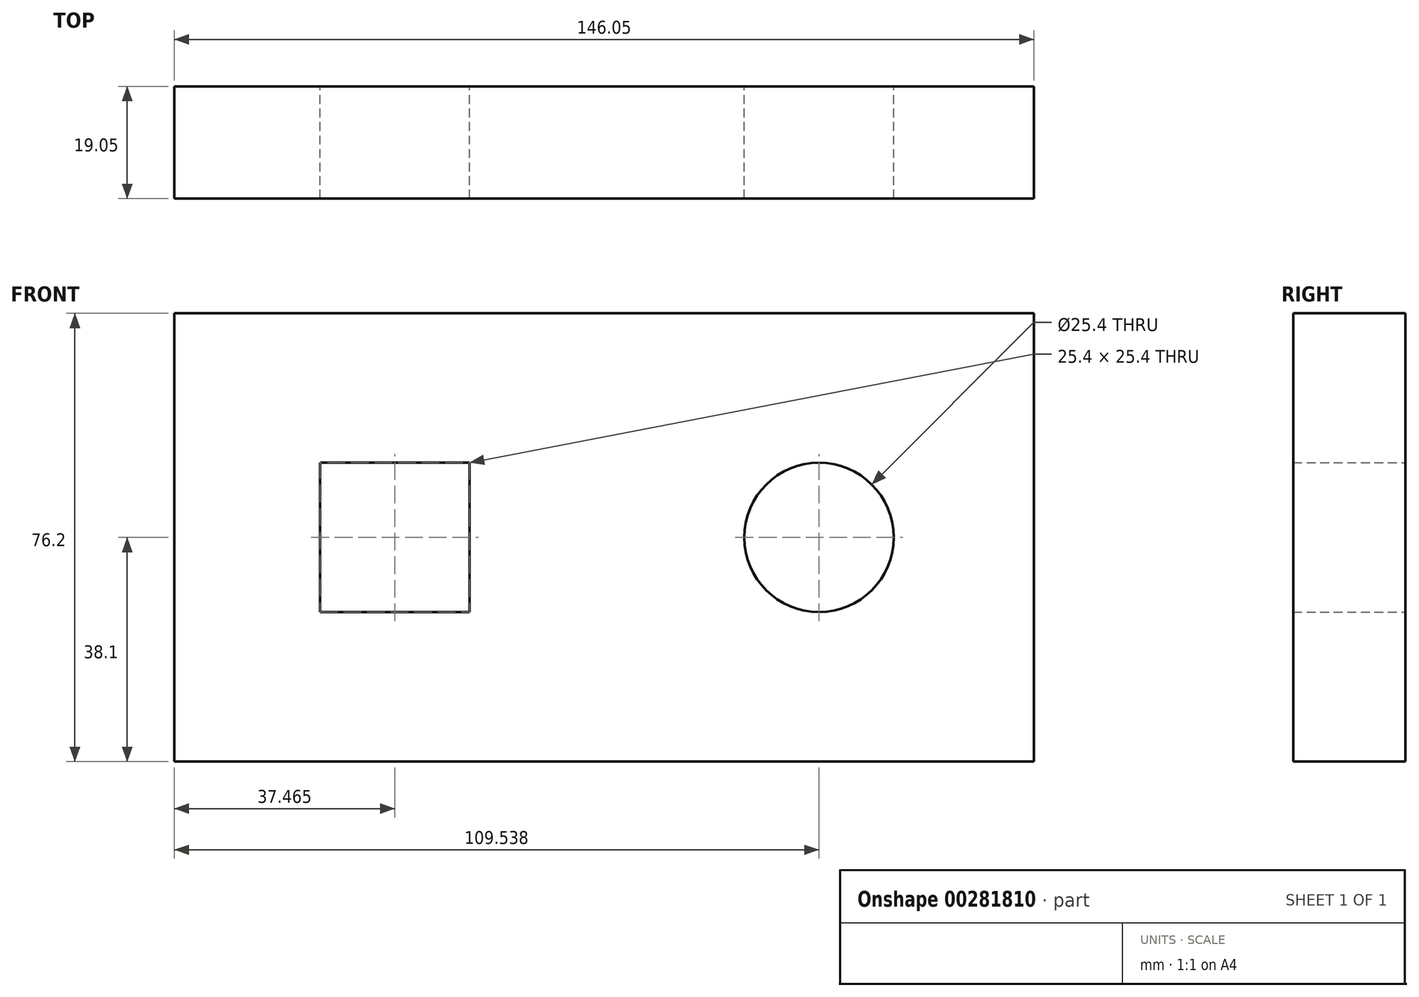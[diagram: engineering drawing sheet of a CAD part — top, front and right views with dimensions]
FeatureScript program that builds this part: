
annotation { "Feature Type Name" : "Feature", "Feature Type Description" : "" }
export const myFeature = defineFeature(function(context is Context, id is Id, definition is map)
    precondition{}
    {
        {
            var Q0;
            Q0=qCreatedBy(makeId("Front.planeOp"),FACE);
            var sketch = newSketch(context, id + "F0", { "sketchPlane" : qUnion([Q0])});
            skLineSegment(sketch, "E0.bottom", {"start": v(0, 0) * mm, "end": v(-146.05, 0) * mm});
            skLineSegment(sketch, "E0.top", {"start": v(0, 76.2) * mm, "end": v(-146.05, 76.2) * mm});
            skLineSegment(sketch, "E0.left", {"start": v(0, 0) * mm, "end": v(0, 76.2) * mm});
            skLineSegment(sketch, "E0.right", {"start": v(-146.05, 0) * mm, "end": v(-146.05, 76.2) * mm});
            skLineSegment(sketch, "E1.bottom", {"start": v(-95.88, 25.4) * mm, "end": v(-121.29, 25.4) * mm});
            skLineSegment(sketch, "E1.top", {"start": v(-95.88, 50.8) * mm, "end": v(-121.29, 50.8) * mm});
            skLineSegment(sketch, "E1.left", {"start": v(-95.88, 25.4) * mm, "end": v(-95.88, 50.8) * mm});
            skLineSegment(sketch, "E1.right", {"start": v(-121.29, 25.4) * mm, "end": v(-121.29, 50.8) * mm});
            skCircle(sketch, "E2", {"center": v(-36.51, 38.1) * mm, "radius": 12.7 * mm});
            skSolve(sketch);
        }
        {
            var Q0;
            Q0 = qSketchRegion(id + "F0", true);
            extrude(context, id + "F1", {"entities" : qUnion([Q0]), "depth" : 19.05 * mm});
        }
    });
